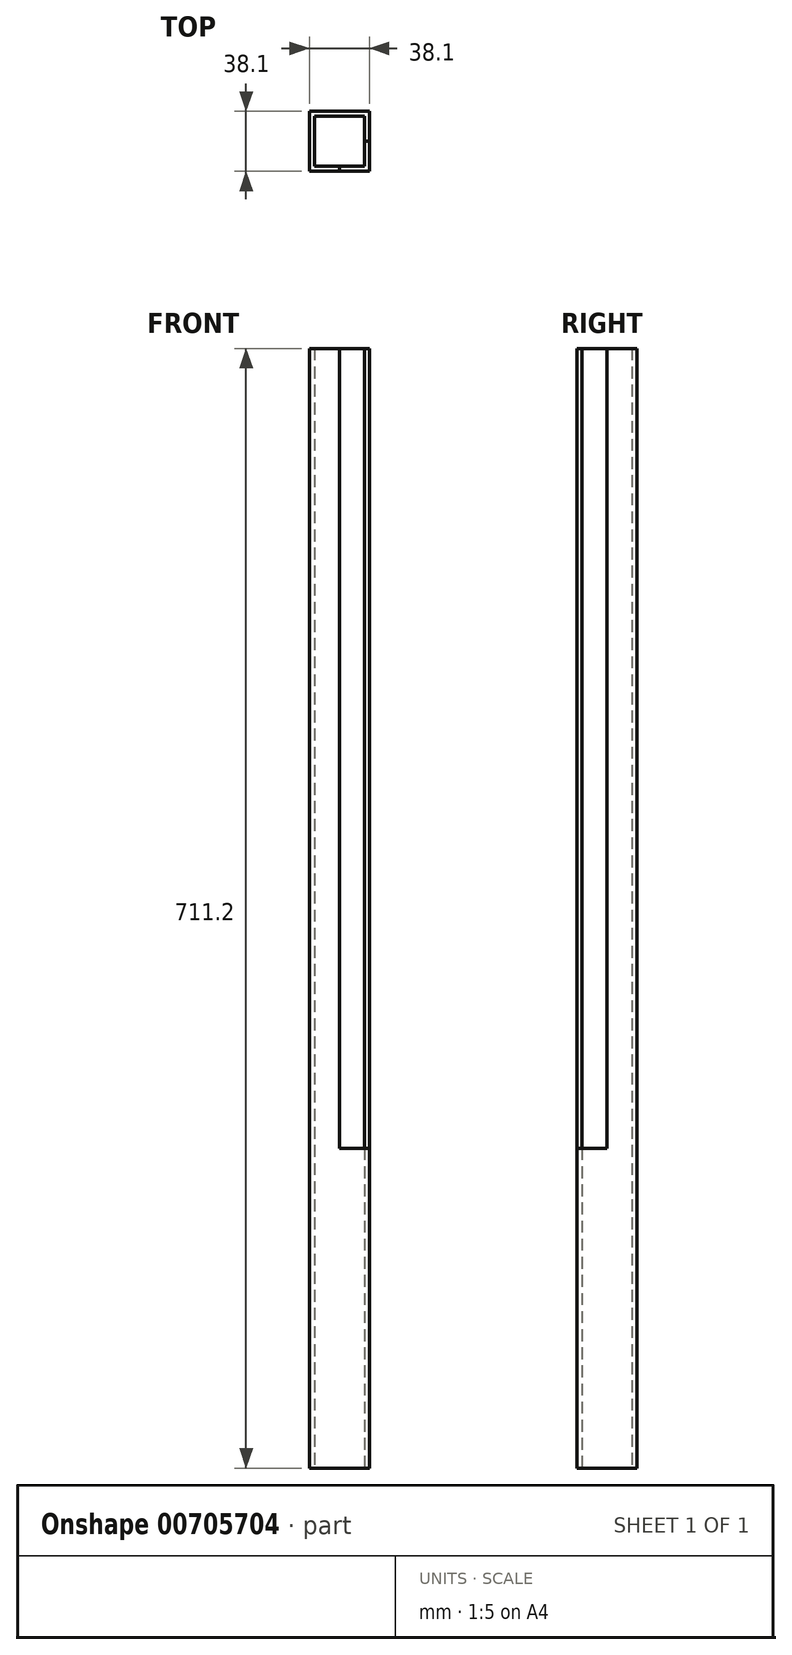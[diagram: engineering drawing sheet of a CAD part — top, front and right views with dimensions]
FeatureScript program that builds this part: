
annotation { "Feature Type Name" : "Feature", "Feature Type Description" : "" }
export const myFeature = defineFeature(function(context is Context, id is Id, definition is map)
    precondition{}
    {
        {
            var Q0;
            Q0=qCreatedBy(makeId("Top.planeOp"),FACE);
            var sketch = newSketch(context, id + "F0", { "sketchPlane" : qUnion([Q0])});
            skLineSegment(sketch, "E0.bottom", {"start": v(0, 0) * mm, "end": v(38.1, 0) * mm});
            skLineSegment(sketch, "E0.top", {"start": v(0, 38.1) * mm, "end": v(38.1, 38.1) * mm});
            skLineSegment(sketch, "E0.left", {"start": v(0, 0) * mm, "end": v(0, 38.1) * mm});
            skLineSegment(sketch, "E0.right", {"start": v(38.1, 0) * mm, "end": v(38.1, 38.1) * mm});
            skSolve(sketch);
        }
        {
            var Q0;
            Q0 = qSketchRegion(id + "F0", true);
            extrude(context, id + "F1", {"entities" : qUnion([Q0]), "depth" : 711.2 * mm, "offsetDistance" : 25.4 * mm});
        }
        {
            var Q0;
            Q0=makeQuery(id+"F1.opExtrude","SWEPT_FACE",FACE,{"disambiguationData":[OSD([sQuery(id+"F0.wireOp",EDGE,"E0.bottom")])]});
            var sketch = newSketch(context, id + "F2", { "sketchPlane" : qUnion([Q0])});
            skLineSegment(sketch, "E1.bottom", {"start": v(38.1, 711.2) * mm, "end": v(19.05, 711.2) * mm});
            skLineSegment(sketch, "E1.top", {"start": v(38.1, 203.2) * mm, "end": v(19.05, 203.2) * mm});
            skLineSegment(sketch, "E1.left", {"start": v(38.1, 711.2) * mm, "end": v(38.1, 203.2) * mm});
            skLineSegment(sketch, "E1.right", {"start": v(19.05, 711.2) * mm, "end": v(19.05, 203.2) * mm});
            skSolve(sketch);
        }
        {
            var Q0;
            Q0 = qSketchRegion(id + "F2", true);
            extrude(context, id + "F3", {"entities" : qUnion([Q0]), "operationType" : NewBodyOperationType.REMOVE, "oppositeDirection" : true, "depth" : 19.05 * mm, "offsetDistance" : 25.4 * mm});
        }
        {
            var Q0;
            Q0=makeQuery(id+"F1.opExtrude","CAP_FACE",FACE,{"disambiguationData":[OSD([sQuery(id+"F0.wireOp",EDGE,"E0.bottom"),sQuery(id+"F0.wireOp",EDGE,"E0.top"),sQuery(id+"F0.wireOp",EDGE,"E0.left"),sQuery(id+"F0.wireOp",EDGE,"E0.right")])],"isStart":true});
            var sketch = newSketch(context, id + "F4", { "sketchPlane" : qUnion([Q0])});
            skLineSegment(sketch, "E2.0", {"start": v(3.18, -3.18) * mm, "end": v(34.93, -3.18) * mm});
            skLineSegment(sketch, "E2.1", {"start": v(3.18, -3.18) * mm, "end": v(3.18, -34.93) * mm});
            skLineSegment(sketch, "E2.2", {"start": v(3.18, -34.93) * mm, "end": v(34.93, -34.93) * mm});
            skLineSegment(sketch, "E2.3", {"start": v(34.93, -3.18) * mm, "end": v(34.93, -34.93) * mm});
            skSolve(sketch);
        }
        {
            var Q0;
            Q0 = qSketchRegion(id + "F4", true);
            extrude(context, id + "F5", {"entities" : qUnion([Q0]), "operationType" : NewBodyOperationType.REMOVE, "endBound" : BoundingType.THROUGH_ALL, "oppositeDirection" : true, "depth" : 25.4 * mm, "offsetDistance" : 25.4 * mm});
        }
    });
